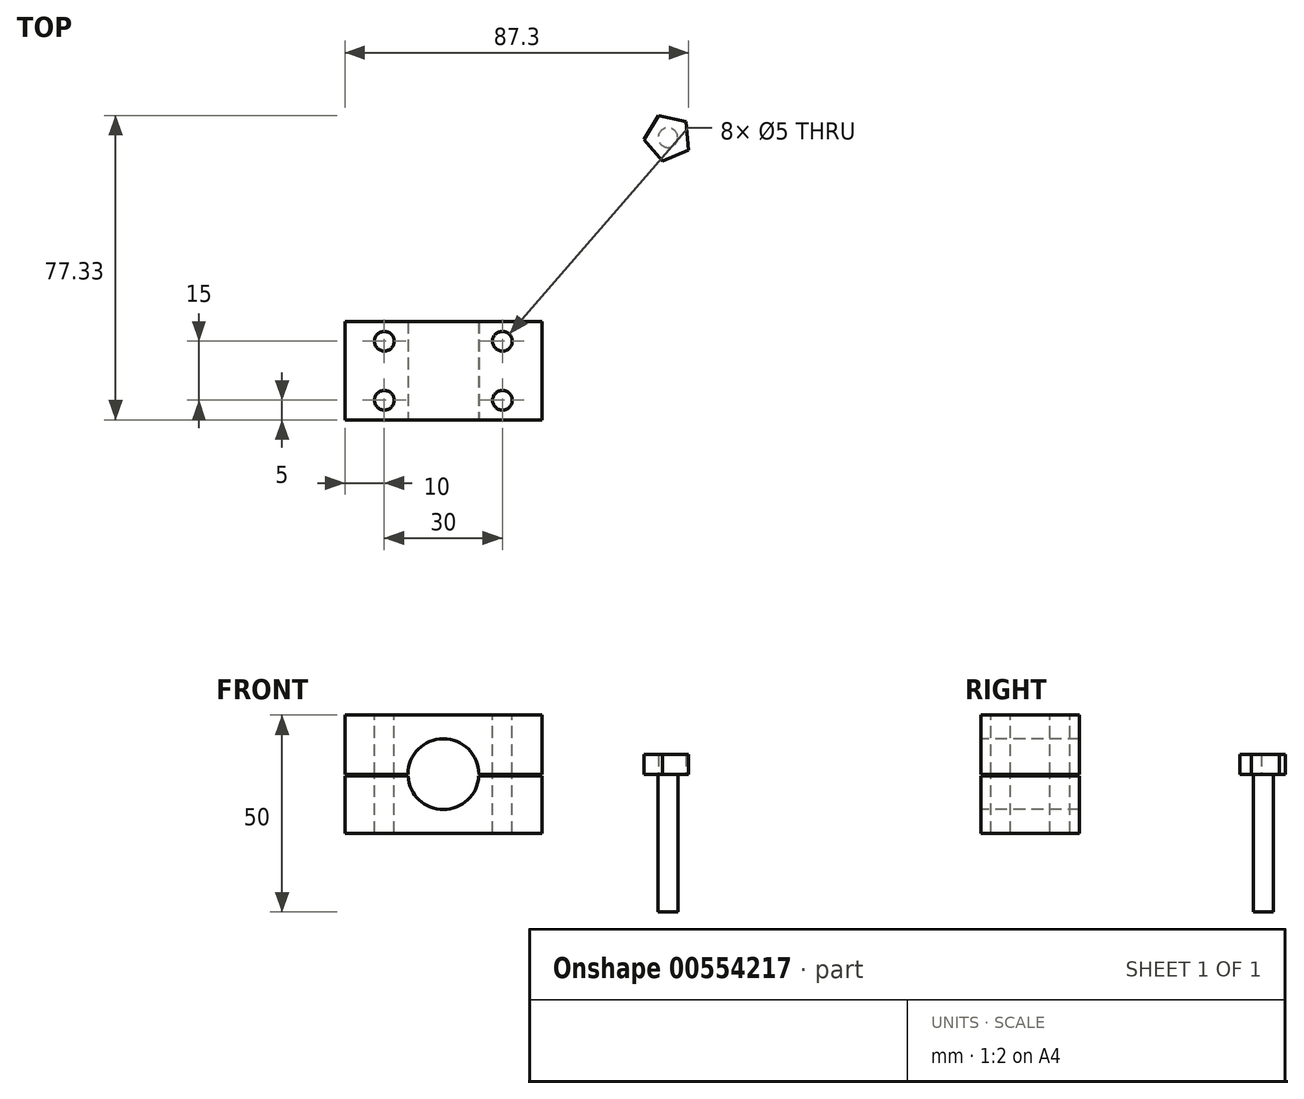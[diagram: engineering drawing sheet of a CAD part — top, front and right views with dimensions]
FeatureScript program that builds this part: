
annotation { "Feature Type Name" : "Feature", "Feature Type Description" : "" }
export const myFeature = defineFeature(function(context is Context, id is Id, definition is map)
    precondition{}
    {
        {
            var Q0;
            Q0=qCreatedBy(makeId("Front.planeOp"),FACE);
            var sketch = newSketch(context, id + "F0", { "sketchPlane" : qUnion([Q0])});
            skLineSegment(sketch, "E0.bottom", {"start": v(-25, 0) * mm, "end": v(25, 0) * mm});
            skLineSegment(sketch, "E0.top", {"start": v(-25, -15) * mm, "end": v(25, -15) * mm});
            skLineSegment(sketch, "E0.left", {"start": v(-25, 0) * mm, "end": v(-25, -15) * mm});
            skLineSegment(sketch, "E0.right", {"start": v(25, 0) * mm, "end": v(25, -15) * mm});
            skSolve(sketch);
        }
        {
            var Q0;
            Q0=makeQuery(id+"F0.imprint","IMPRINT",FACE,{"disambiguationData":[TD([[makeQuery(id+"F0.imprint","IMPRINT",EDGE,{"derivedFrom":sQuery(id+"F0.wireOp",EDGE,"E0.bottom")}),-1.0]])]});
            extrude(context, id + "F1", {"entities" : qUnion([Q0]), "depth" : 25 * mm, "offsetDistance" : 25 * mm});
        }
        {
            var Q0;
            Q0=qCreatedBy(makeId("Front.planeOp"),FACE);
            var sketch = newSketch(context, id + "F2", { "sketchPlane" : qUnion([Q0])});
            skLineSegment(sketch, "E1.bottom", {"start": v(-25, 0) * mm, "end": v(25, 0) * mm});
            skLineSegment(sketch, "E1.top", {"start": v(-25, 15) * mm, "end": v(25, 15) * mm});
            skLineSegment(sketch, "E1.left", {"start": v(-25, 0) * mm, "end": v(-25, 15) * mm});
            skLineSegment(sketch, "E1.right", {"start": v(25, 0) * mm, "end": v(25, 15) * mm});
            skSolve(sketch);
        }
        {
            var Q0;
            Q0 = qSketchRegion(id + "F2", true);
            extrude(context, id + "F3", {"entities" : qUnion([Q0]), "operationType" : NewBodyOperationType.ADD, "depth" : 25 * mm, "offsetDistance" : 25 * mm});
        }
        {
            var Q0;
            Q0=makeQuery(id+"F3.boolean.opBoolean","MERGE",FACE,{"derivedFrom":[makeQuery(id+"F1.opExtrude","CAP_FACE",FACE,{"disambiguationData":[OSD([sQuery(id+"F0.wireOp",EDGE,"E0.bottom"),sQuery(id+"F0.wireOp",EDGE,"E0.top"),sQuery(id+"F0.wireOp",EDGE,"E0.left"),sQuery(id+"F0.wireOp",EDGE,"E0.right")])],"isStart":false}),makeQuery(id+"F3.opExtrude","CAP_FACE",FACE,{"disambiguationData":[OSD([sQuery(id+"F2.wireOp",EDGE,"E1.bottom"),sQuery(id+"F2.wireOp",EDGE,"E1.top"),sQuery(id+"F2.wireOp",EDGE,"E1.left"),sQuery(id+"F2.wireOp",EDGE,"E1.right")])],"isStart":false})]});
            var sketch = newSketch(context, id + "F4", { "sketchPlane" : qUnion([Q0])});
            skCircle(sketch, "E2", {"center": v(0, 0) * mm, "radius": 9 * mm});
            skSolve(sketch);
        }
        {
            var Q0;
            Q0=makeQuery(id+"F4.imprint","IMPRINT",FACE,{"disambiguationData":[TD([[makeQuery(id+"F4.imprint","IMPRINT",EDGE,{"derivedFrom":sQuery(id+"F4.wireOp",EDGE,"E2")}),1.0]])]});
            extrude(context, id + "F5", {"entities" : qUnion([Q0]), "operationType" : NewBodyOperationType.REMOVE, "endBound" : BoundingType.THROUGH_ALL, "oppositeDirection" : true, "depth" : 25 * mm, "offsetDistance" : 25 * mm});
        }
        {
            var Q0;
            Q0=qCreatedBy(makeId("Top.planeOp"),FACE);
            var sketch = newSketch(context, id + "F6", { "sketchPlane" : qUnion([Q0])});
            skLineSegment(sketch, "E3.bottom", {"start": v(42.36, -36.58) * mm, "end": v(-42.36, -36.58) * mm});
            skLineSegment(sketch, "E3.top", {"start": v(42.36, 36.58) * mm, "end": v(-42.36, 36.58) * mm});
            skLineSegment(sketch, "E3.left", {"start": v(42.36, -36.58) * mm, "end": v(42.36, 36.58) * mm});
            skLineSegment(sketch, "E3.right", {"start": v(-42.36, -36.58) * mm, "end": v(-42.36, 36.58) * mm});
            skPoint(sketch, "E3.middle", {"position": v(0, 0) * mm});
            skSolve(sketch);
        }
        {
            var Q0;
            Q0=makeQuery(id+"F6.imprint","IMPRINT",FACE,{"disambiguationData":[TD([[makeQuery(id+"F6.imprint","IMPRINT",EDGE,{"derivedFrom":sQuery(id+"F6.wireOp",EDGE,"E3.bottom")}),-1.0]])]});
            extrude(context, id + "F7", {"entities" : qUnion([Q0]), "operationType" : NewBodyOperationType.REMOVE, "oppositeDirection" : true, "depth" : .5 * mm, "offsetDistance" : 25 * mm});
        }
        {
            var Q0;
            Q0=makeQuery(id+"F3.opExtrude","SWEPT_FACE",FACE,{"disambiguationData":[OSD([sQuery(id+"F2.wireOp",EDGE,"E1.top")])]});
            var sketch = newSketch(context, id + "F8", { "sketchPlane" : qUnion([Q0])});
            skLineSegment(sketch, "E4.bottom", {"start": v(15, -20) * mm, "end": v(-15, -20) * mm, "construction": true});
            skLineSegment(sketch, "E4.top", {"start": v(15, -5) * mm, "end": v(-15, -5) * mm, "construction": true});
            skLineSegment(sketch, "E4.left", {"start": v(15, -20) * mm, "end": v(15, -5) * mm, "construction": true});
            skLineSegment(sketch, "E4.right", {"start": v(-15, -20) * mm, "end": v(-15, -5) * mm, "construction": true});
            skPoint(sketch, "E4.middle", {"position": v(0, -12.5) * mm});
            skPoint(sketch, "E4.middle.positionSnap0", {"position": v(-25, -12.5) * mm});
            skPoint(sketch, "E4.centerSnap0", {"position": v(-25, -12.5) * mm});
            skLineSegment(sketch, "E5.bottom", {"start": v(-9, -5) * mm, "end": v(9, -5) * mm, "construction": true});
            skLineSegment(sketch, "E5.top", {"start": v(-9, -20) * mm, "end": v(9, -20) * mm, "construction": true});
            skLineSegment(sketch, "E5.left", {"start": v(-9, -5) * mm, "end": v(-9, -20) * mm, "construction": true});
            skLineSegment(sketch, "E5.right", {"start": v(9, -5) * mm, "end": v(9, -20) * mm, "construction": true});
            skSolve(sketch);
        }
        {
            var Q0;
            Q0=sQuery(id+"F8.wireOp",VERTEX,"E4.right.end");
            var Q1;
            Q1=sQuery(id+"F8.wireOp",VERTEX,"E4.right.start");
            var Q2;
            Q2=sQuery(id+"F8.wireOp",VERTEX,"E4.left.end");
            var Q3;
            Q3=sQuery(id+"F8.wireOp",VERTEX,"E4.bottom.start");
            var Q4;
            Q4=makeQuery(id+"F7.boolean.opBoolean","SPLIT",BODY,{"disambiguationData":[OD(0.0)],"derivedFrom":makeQuery(id+"F1.opExtrude","SWEPT_BODY",BODY,{"disambiguationData":[OSD([sQuery(id+"F0.wireOp",EDGE,"E0.bottom"),sQuery(id+"F0.wireOp",EDGE,"E0.top"),sQuery(id+"F0.wireOp",EDGE,"E0.left"),sQuery(id+"F0.wireOp",EDGE,"E0.right")])]})});
            var Q5;
            Q5=makeQuery(id+"F7.boolean.opBoolean","SPLIT",BODY,{"disambiguationData":[OD(1.0)],"derivedFrom":makeQuery(id+"F1.opExtrude","SWEPT_BODY",BODY,{"disambiguationData":[OSD([sQuery(id+"F0.wireOp",EDGE,"E0.bottom"),sQuery(id+"F0.wireOp",EDGE,"E0.top"),sQuery(id+"F0.wireOp",EDGE,"E0.left"),sQuery(id+"F0.wireOp",EDGE,"E0.right")])]})});
            hole(context, id + "F9", {"style" : HoleStyle.SIMPLE, "endStyle" : HoleEndStyle.THROUGH, "holeDiameter" : 5 * mm, "isTappedThrough" : true, "tappedDepth" : 12 * mm, "tapClearance" : 3, "locations" : qUnion([Q0, Q1, Q2, Q3]), "scope" : qUnion([Q4, Q5])});
        }
        {
            var Q0;
            Q0=qCreatedBy(makeId("Top.planeOp"),FACE);
            var sketch = newSketch(context, id + "F10", { "sketchPlane" : qUnion([Q0])});
            skCircle(sketch, "E6", {"center": v(57.05, 46.73) * mm, "radius": 2.5 * mm});
            skSolve(sketch);
        }
        {
            var Q0;
            Q0=makeQuery(id+"F10.imprint","IMPRINT",FACE,{"disambiguationData":[TD([[makeQuery(id+"F10.imprint","IMPRINT",EDGE,{"derivedFrom":sQuery(id+"F10.wireOp",EDGE,"E6")}),1.0]])]});
            extrude(context, id + "F11", {"entities" : qUnion([Q0]), "oppositeDirection" : true, "depth" : 35 * mm, "offsetDistance" : 25 * mm});
        }
        {
            var Q0;
            Q0=makeQuery(id+"F11.opExtrude","CAP_FACE",FACE,{"disambiguationData":[OSD([sQuery(id+"F10.wireOp",EDGE,"E6")])],"isStart":true});
            var sketch = newSketch(context, id + "F12", { "sketchPlane" : qUnion([Q0])});
            skCircle(sketch, "E7.cCircle", {"center": v(57.05, 46.73) * mm, "radius": 4.94 * mm, "construction": true});
            skLineSegment(sketch, "E7.0", {"start": v(50.98, 46.17) * mm, "end": v(54.65, 52.33) * mm});
            skLineSegment(sketch, "E7.1", {"start": v(54.65, 52.33) * mm, "end": v(61.64, 50.75) * mm});
            skLineSegment(sketch, "E7.2", {"start": v(61.64, 50.75) * mm, "end": v(62.3, 43.6) * mm});
            skLineSegment(sketch, "E7.3", {"start": v(62.3, 43.6) * mm, "end": v(55.7, 40.78) * mm});
            skLineSegment(sketch, "E7.4", {"start": v(55.7, 40.78) * mm, "end": v(50.98, 46.17) * mm});
            skPoint(sketch, "E7.0.midPoint", {"position": v(52.81, 49.25) * mm});
            skSolve(sketch);
        }
        {
            var Q0;
            Q0=makeQuery(id+"F12.imprint","IMPRINT",FACE,{"disambiguationData":[TD([[makeQuery(id+"F12.imprint","IMPRINT",EDGE,{"derivedFrom":sQuery(id+"F12.wireOp",EDGE,"E7.0")}),-1.0]])]});
            var Q1;
            Q1=makeQuery(id+"F12.imprint","IMPRINT",FACE,{"disambiguationData":[TD([[makeQuery(id+"F12.imprint","IMPRINT",EDGE,{"derivedFrom":makeQuery(id+"F11.opExtrude","CAP_EDGE",EDGE,{"disambiguationData":[OSD([sQuery(id+"F10.wireOp",EDGE,"E6")])],"isStart":true})}),1.0]])]});
            extrude(context, id + "F13", {"entities" : qUnion([Q0, Q1]), "operationType" : NewBodyOperationType.ADD, "depth" : 5 * mm, "offsetDistance" : 25 * mm});
        }
    });
